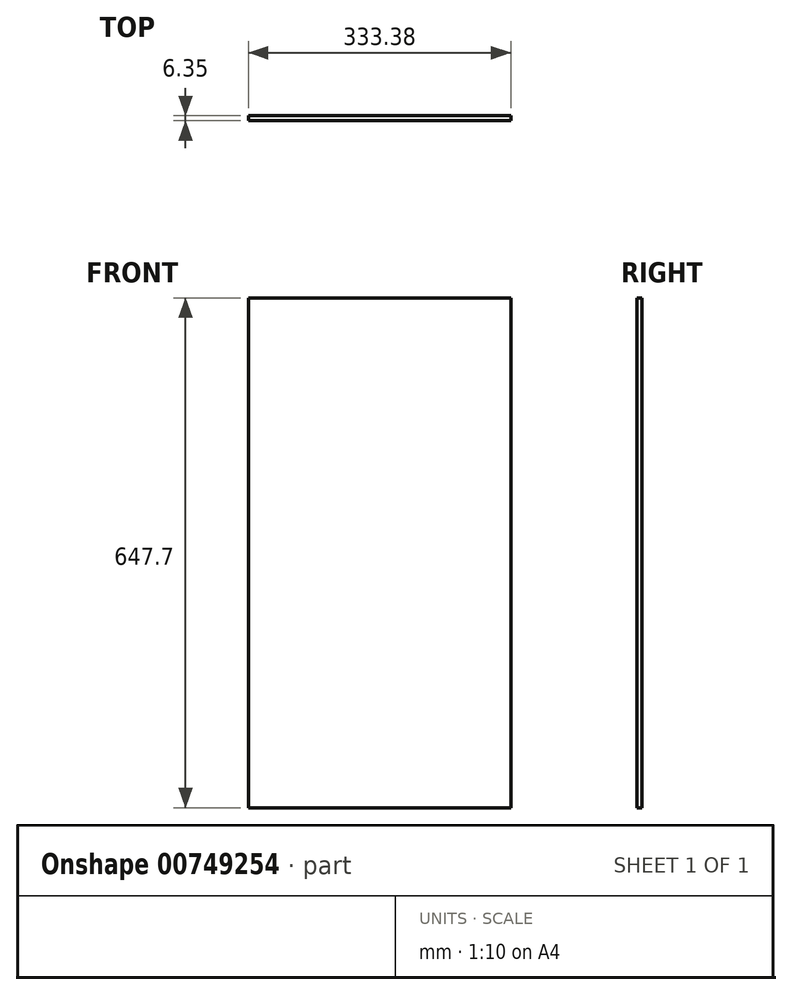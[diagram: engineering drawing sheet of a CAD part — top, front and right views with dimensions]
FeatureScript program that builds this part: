
annotation { "Feature Type Name" : "Feature", "Feature Type Description" : "" }
export const myFeature = defineFeature(function(context is Context, id is Id, definition is map)
    precondition{}
    {
        {
            var Q0;
            Q0=qCreatedBy(makeId("Front.planeOp"),FACE);
            var sketch = newSketch(context, id + "F0", { "sketchPlane" : qUnion([Q0])});
            skLineSegment(sketch, "E0.bottom", {"start": v(166.69, 323.85) * mm, "end": v(-166.69, 323.85) * mm});
            skLineSegment(sketch, "E0.top", {"start": v(166.69, -323.85) * mm, "end": v(-166.69, -323.85) * mm});
            skLineSegment(sketch, "E0.left", {"start": v(166.69, 323.85) * mm, "end": v(166.69, -323.85) * mm});
            skLineSegment(sketch, "E0.right", {"start": v(-166.69, 323.85) * mm, "end": v(-166.69, -323.85) * mm});
            skPoint(sketch, "E0.middle", {"position": v(0, 0) * mm});
            skSolve(sketch);
        }
        {
            var Q0;
            Q0=qSketchRegion(id+"F0",true);
            extrude(context, id + "F1", {"entities" : qUnion([Q0]), "depth" : 6.35 * mm, "offsetDistance" : 25.4 * mm});
        }
    });
